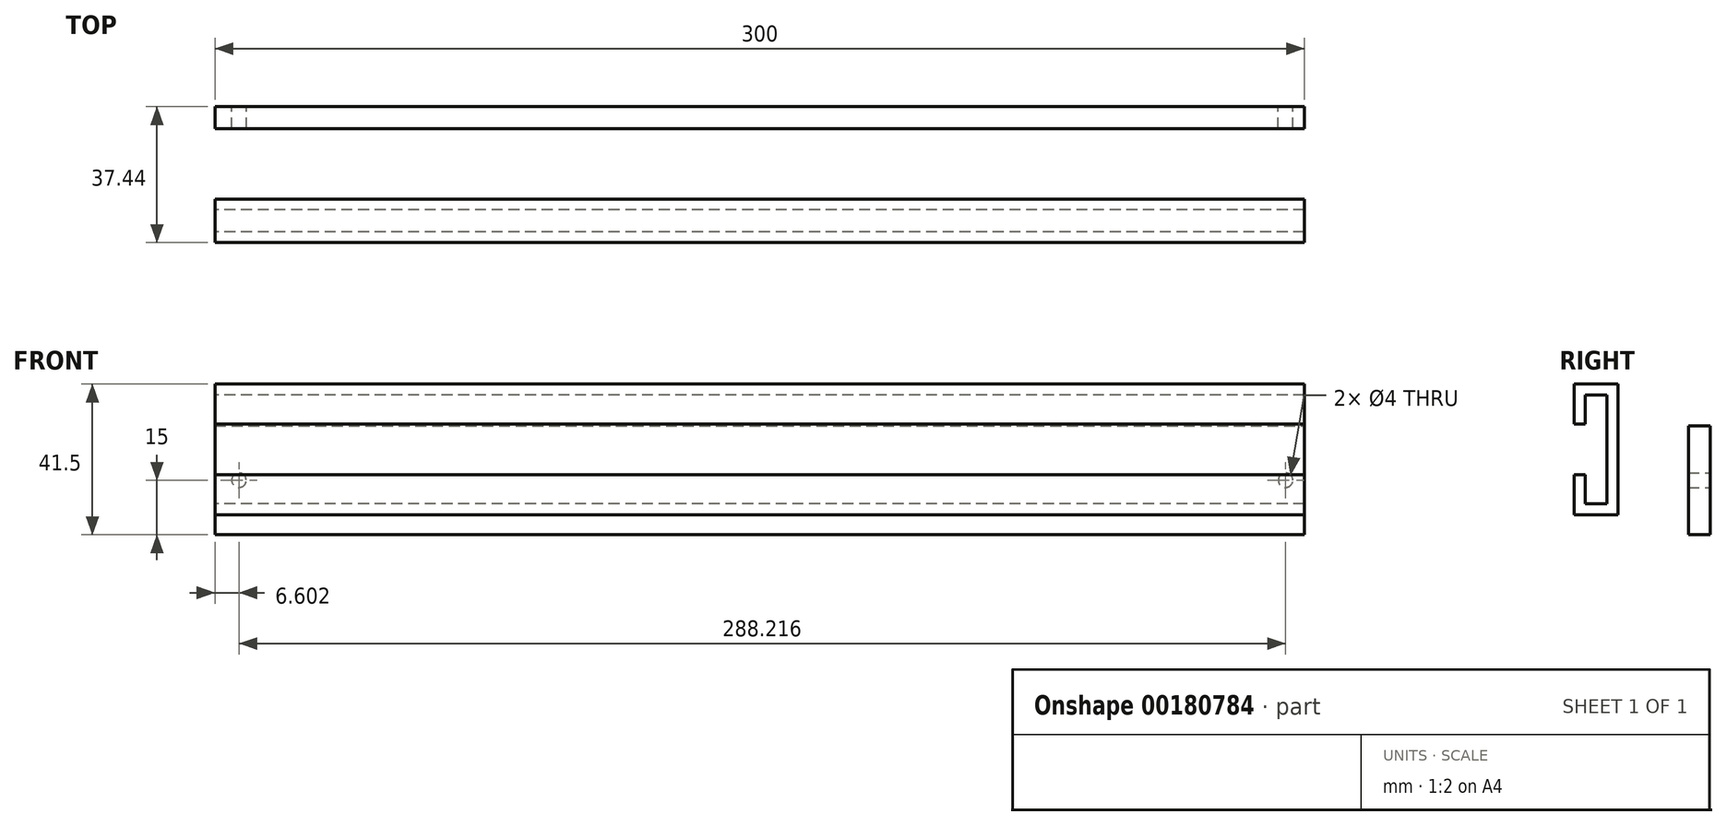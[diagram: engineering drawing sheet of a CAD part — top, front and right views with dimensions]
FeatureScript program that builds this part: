
annotation { "Feature Type Name" : "Feature", "Feature Type Description" : "" }
export const myFeature = defineFeature(function(context is Context, id is Id, definition is map)
    precondition{}
    {
        {
            var Q0;
            Q0=qCreatedBy(makeId("Front.planeOp"),FACE);
            var sketch = newSketch(context, id + "F0", { "sketchPlane" : qUnion([Q0])});
            skLineSegment(sketch, "E0.bottom", {"start": v(0, 0) * mm, "end": v(300, 0) * mm});
            skLineSegment(sketch, "E0.top", {"start": v(0, 30) * mm, "end": v(300, 30) * mm});
            skLineSegment(sketch, "E0.left", {"start": v(0, 0) * mm, "end": v(0, 30) * mm});
            skLineSegment(sketch, "E0.right", {"start": v(300, 0) * mm, "end": v(300, 30) * mm});
            skCircle(sketch, "E1", {"center": v(6.6, 15) * mm, "radius": 2 * mm});
            skPoint(sketch, "E1.centerSnap0", {"position": v(0, 15) * mm});
            skCircle(sketch, "E2", {"center": v(294.82, 15) * mm, "radius": 2 * mm});
            skPoint(sketch, "E2.centerSnap0", {"position": v(300, 15) * mm});
            skSolve(sketch);
        }
        {
            var Q0;
            Q0=makeQuery(id+"F0.imprint","IMPRINT",FACE,{"disambiguationData":[TD([[makeQuery(id+"F0.imprint","IMPRINT",EDGE,{"derivedFrom":sQuery(id+"F0.wireOp",EDGE,"E0.bottom")}),1.0]])]});
            extrude(context, id + "F1", {"entities" : qUnion([Q0]), "depth" : 6 * mm});
        }
        {
            var Q0;
            Q0=qCreatedBy(makeId("Right.planeOp"),FACE);
            var sketch = newSketch(context, id + "F2", { "sketchPlane" : qUnion([Q0])});
            skLineSegment(sketch, "E3", {"start": v(-25.44, 5.5) * mm, "end": v(-25.44, 41.5) * mm});
            skLineSegment(sketch, "E4", {"start": v(-25.44, 41.5) * mm, "end": v(-37.44, 41.5) * mm});
            skLineSegment(sketch, "E5", {"start": v(-37.44, 41.5) * mm, "end": v(-37.44, 30.5) * mm});
            skLineSegment(sketch, "E6", {"start": v(-25.44, 5.5) * mm, "end": v(-37.44, 5.5) * mm});
            skLineSegment(sketch, "E7", {"start": v(-37.44, 5.5) * mm, "end": v(-37.44, 16.5) * mm});
            skLineSegment(sketch, "E8", {"start": v(-37.44, 16.5) * mm, "end": v(-34.44, 16.5) * mm});
            skLineSegment(sketch, "E9", {"start": v(-34.44, 16.5) * mm, "end": v(-34.44, 8.5) * mm});
            skLineSegment(sketch, "E10", {"start": v(-34.44, 8.5) * mm, "end": v(-28.44, 8.5) * mm});
            skLineSegment(sketch, "E11", {"start": v(-28.44, 8.5) * mm, "end": v(-28.44, 38.5) * mm});
            skLineSegment(sketch, "E12", {"start": v(-28.44, 38.5) * mm, "end": v(-34.44, 38.5) * mm});
            skLineSegment(sketch, "E13", {"start": v(-34.44, 38.5) * mm, "end": v(-34.44, 30.5) * mm});
            skLineSegment(sketch, "E14", {"start": v(-37.44, 30.5) * mm, "end": v(-34.44, 30.5) * mm});
            skSolve(sketch);
        }
        {
            var Q0;
            Q0=makeQuery(id+"F2.imprint","IMPRINT",FACE,{"disambiguationData":[TD([[makeQuery(id+"F2.imprint","IMPRINT",EDGE,{"derivedFrom":sQuery(id+"F2.wireOp",EDGE,"E3")}),1.0]])]});
            extrude(context, id + "F3", {"entities" : qUnion([Q0]), "depth" : 300 * mm});
        }
    });
